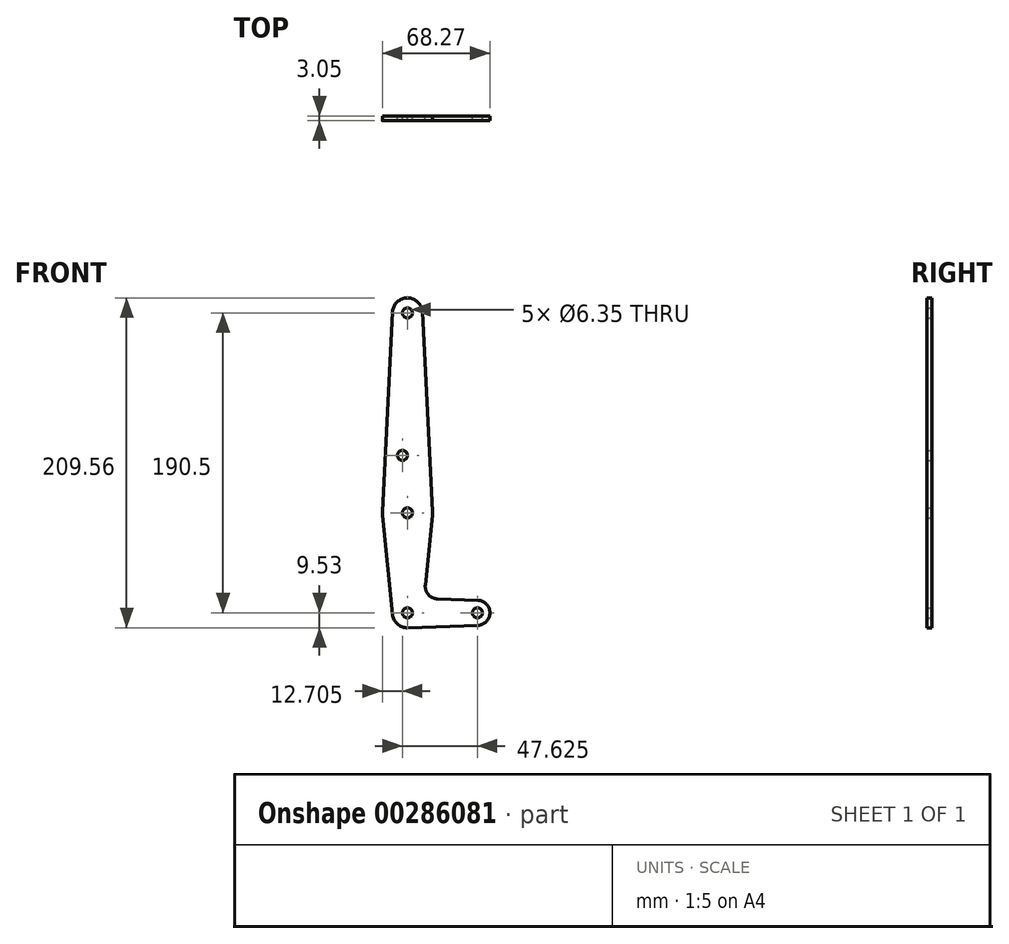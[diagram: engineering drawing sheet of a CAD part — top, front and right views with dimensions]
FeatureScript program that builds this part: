
annotation { "Feature Type Name" : "Feature", "Feature Type Description" : "" }
export const myFeature = defineFeature(function(context is Context, id is Id, definition is map)
    precondition{}
    {
        {
            var Q0;
            Q0=qCreatedBy(makeId("Front.planeOp"),FACE);
            var sketch = newSketch(context, id + "F0", { "sketchPlane" : qUnion([Q0])});
            skCircle(sketch, "E0", {"center": v(0, 0) * mm, "radius": 15.88 * mm});
            skLineSegment(sketch, "E1", {"start": v(0, 127) * mm, "end": v(0, -63.5) * mm, "construction": true});
            skLineSegment(sketch, "E2", {"start": v(0, -63.5) * mm, "end": v(44.45, -63.5) * mm, "construction": true});
            skCircle(sketch, "E3", {"center": v(0, 127) * mm, "radius": 9.53 * mm});
            skCircle(sketch, "E4", {"center": v(0, -63.5) * mm, "radius": 9.53 * mm});
            skCircle(sketch, "E5", {"center": v(44.45, -63.5) * mm, "radius": 7.94 * mm});
            skCircle(sketch, "E6", {"center": v(0, 127) * mm, "radius": 3.18 * mm});
            skCircle(sketch, "E7", {"center": v(0, -63.5) * mm, "radius": 3.18 * mm});
            skCircle(sketch, "E8", {"center": v(44.45, -63.5) * mm, "radius": 3.18 * mm});
            skCircle(sketch, "E9", {"center": v(-3.17, 36.53) * mm, "radius": 3.18 * mm});
            skCircle(sketch, "E10", {"center": v(0, 0) * mm, "radius": 3.18 * mm});
            skLineSegment(sketch, "E11", {"start": v(44.73, -71.43) * mm, "end": v(0.34, -73.02) * mm});
            skLineSegment(sketch, "E12", {"start": v(9.51, 127.48) * mm, "end": v(15.86, 0.8) * mm});
            skLineSegment(sketch, "E13", {"start": v(-9.48, -64.45) * mm, "end": v(-15.8, -1.59) * mm});
            skLineSegment(sketch, "E14", {"start": v(-15.86, 0.8) * mm, "end": v(-9.51, 127.48) * mm});
            skLineSegment(sketch, "E15", {"start": v(15.8, -1.59) * mm, "end": v(9.48, -64.45) * mm});
            skLineSegment(sketch, "E16", {"start": v(0.34, -53.98) * mm, "end": v(44.73, -55.57) * mm});
            skArc(sketch, "E17", {"start": v(11.34, -45.9) * mm, "mid": v(13.26, -51.93) * mm, "end": v(18.97, -54.65) * mm});
            skSolve(sketch);
        }
        {
            var Q0;
            Q0 = qSketchRegion(id + "F0", true);
            var Q1;
            {var subQ0=sQuery(id+"F0.wireOp",EDGE,"E15");var subQ1=sQuery(id+"F0.wireOp",EDGE,"E4");var subQ2=makeQuery(id+"F0.imprint","INTERSECT",VERTEX,{"derivedFrom":[subQ1,subQ0]});Q1=makeQuery(id+"F0.imprint","IMPRINT",FACE,{"disambiguationData":[TD([[makeQuery(id+"F0.imprint","IMPRINT",EDGE,{"disambiguationData":[TD([[subQ2,-1.0]])],"derivedFrom":subQ1}),-1.0]])]});}
            extrude(context, id + "F1", {"entities" : qUnion([Q0, Q1]), "depth" : 3.05 * mm});
        }
    });
